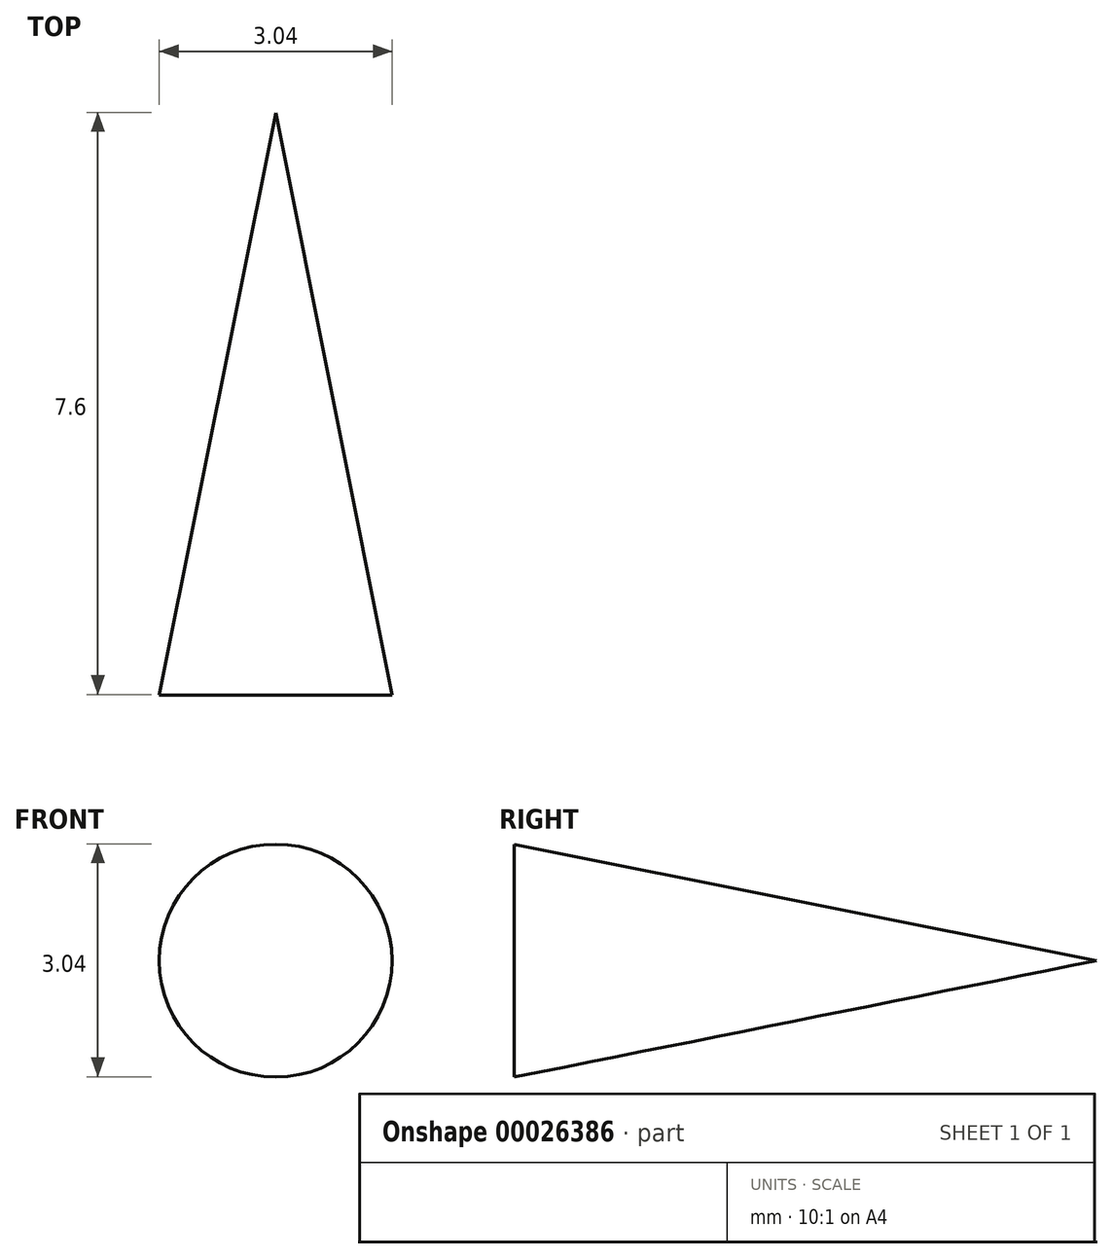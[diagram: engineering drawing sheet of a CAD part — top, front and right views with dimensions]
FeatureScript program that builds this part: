
annotation { "Feature Type Name" : "Feature", "Feature Type Description" : "" }
export const myFeature = defineFeature(function(context is Context, id is Id, definition is map)
    precondition{}
    {
        {
            var Q0;
            Q0=qCreatedBy(makeId("Right.planeOp"),FACE);
            var sketch = newSketch(context, id + "F0", { "sketchPlane" : qUnion([Q0])});
            skLineSegment(sketch, "E0", {"start": v(3.79, 0) * mm, "end": v(3.79, -2.77) * mm});
            skLineSegment(sketch, "E1", {"start": v(3.79, -2.77) * mm, "end": v(11.39, -1.25) * mm});
            skLineSegment(sketch, "E2", {"start": v(11.39, -1.25) * mm, "end": v(3.79, 0) * mm});
            skLineSegment(sketch, "E3", {"start": v(11.39, -1.25) * mm, "end": v(3.79, -1.25) * mm});
            skSolve(sketch);
        }
        {
            var Q0;
            {var subQ1=sQuery(id+"F0.wireOp",EDGE,"E1");Q0=makeQuery(id+"F0.imprint","IMPRINT",FACE,{"disambiguationData":[TD([[makeQuery(id+"F0.imprint","IMPRINT",EDGE,{"derivedFrom":subQ1}),1.0]])]});}
            var Q1;
            Q1=sQuery(id+"F0.wireOp",EDGE,"E3");
            revolve(context, id + "F1", {"entities" : qUnion([Q0]), "axis" : qUnion([Q1]), "revolveType" : RevolveType.FULL});
        }
    });
